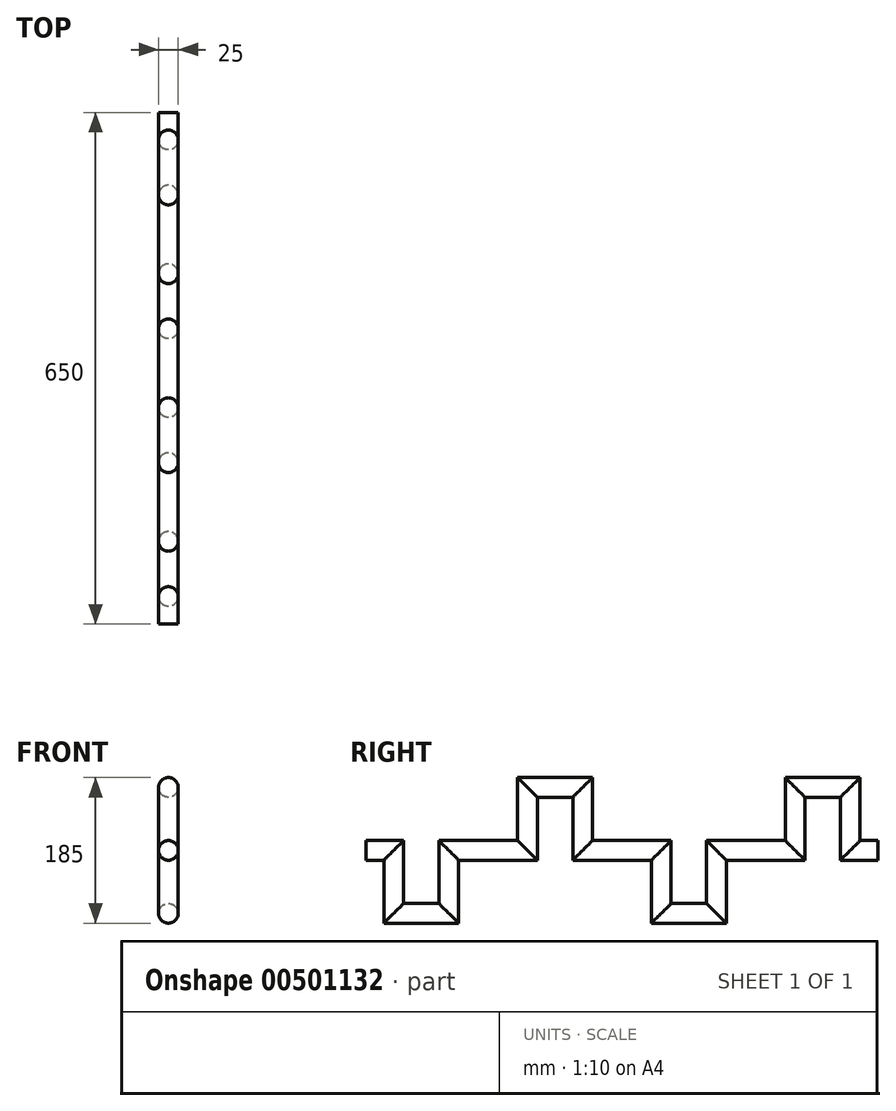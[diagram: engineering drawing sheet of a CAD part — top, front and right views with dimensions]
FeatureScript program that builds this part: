
annotation { "Feature Type Name" : "Feature", "Feature Type Description" : "" }
export const myFeature = defineFeature(function(context is Context, id is Id, definition is map)
    precondition{}
    {
        {
            var Q0;
            Q0=qCreatedBy(makeId("Right.planeOp"),FACE);
            var sketch = newSketch(context, id + "F0", { "sketchPlane" : qUnion([Q0])});
            skLineSegment(sketch, "E0", {"start": v(-325, 0) * mm, "end": v(-290, 0) * mm});
            skLineSegment(sketch, "E1", {"start": v(-290, 0) * mm, "end": v(-290, -80) * mm});
            skLineSegment(sketch, "E2", {"start": v(-290, -80) * mm, "end": v(-220, -80) * mm});
            skLineSegment(sketch, "E3", {"start": v(-220, -80) * mm, "end": v(-220, 0) * mm});
            skLineSegment(sketch, "E4", {"start": v(-220, 0) * mm, "end": v(-120, 0) * mm});
            skLineSegment(sketch, "E5", {"start": v(-120, 0) * mm, "end": v(-120, 80) * mm});
            skLineSegment(sketch, "E6", {"start": v(-120, 80) * mm, "end": v(-50, 80) * mm});
            skLineSegment(sketch, "E7", {"start": v(-50, 80) * mm, "end": v(-50, 0) * mm});
            skLineSegment(sketch, "E8", {"start": v(-50, 0) * mm, "end": v(50, 0) * mm});
            skLineSegment(sketch, "E9", {"start": v(50, 0) * mm, "end": v(50, -80) * mm});
            skLineSegment(sketch, "E10", {"start": v(50, -80) * mm, "end": v(120, -80) * mm});
            skLineSegment(sketch, "E11", {"start": v(120, -80) * mm, "end": v(120, 0) * mm});
            skLineSegment(sketch, "E12", {"start": v(120, 0) * mm, "end": v(220, 0) * mm});
            skLineSegment(sketch, "E13", {"start": v(220, 0) * mm, "end": v(220, 80) * mm});
            skLineSegment(sketch, "E14", {"start": v(220, 80) * mm, "end": v(290, 80) * mm});
            skLineSegment(sketch, "E15", {"start": v(290, 80) * mm, "end": v(290, 0) * mm});
            skLineSegment(sketch, "E16", {"start": v(290, 0) * mm, "end": v(325, 0) * mm});
            skSolve(sketch);
        }
        {
            var Q0;
            Q0=qCreatedBy(makeId("Front.planeOp"),FACE);
            var Q1;
            Q1=sQuery(id+"F0.wireOp",VERTEX,"E0.start");
            cPlane(context, id + "F1", {"entities" : qUnion([Q0, Q1]), "cplaneType" : CPlaneType.PLANE_POINT, "offset" : 25 * mm, "width" : 150 * mm, "height" : 150 * mm});
        }
        {
            var Q0;
            Q0=qCreatedBy(id+"F1.planeOp",FACE);
            var sketch = newSketch(context, id + "F2", { "sketchPlane" : qUnion([Q0])});
            skCircle(sketch, "E17", {"center": v(0, 0) * mm, "radius": 12.5 * mm});
            skSolve(sketch);
        }
        {
            var Q0;
            Q0=makeQuery(id+"F2.imprint","IMPRINT",FACE,{"disambiguationData":[TD([[makeQuery(id+"F2.imprint","IMPRINT",EDGE,{"derivedFrom":sQuery(id+"F2.wireOp",EDGE,"E17")}),1.0]])]});
            var Q1;
            Q1 = qConstructionFilter(qBodyType(qCreatedBy(id + "F0" ,EDGE), BodyType.WIRE), ConstructionObject.NO);
            sweep(context, id + "F3", {"profiles" : qUnion([Q0]), "path" : qUnion([Q1])});
        }
    });
